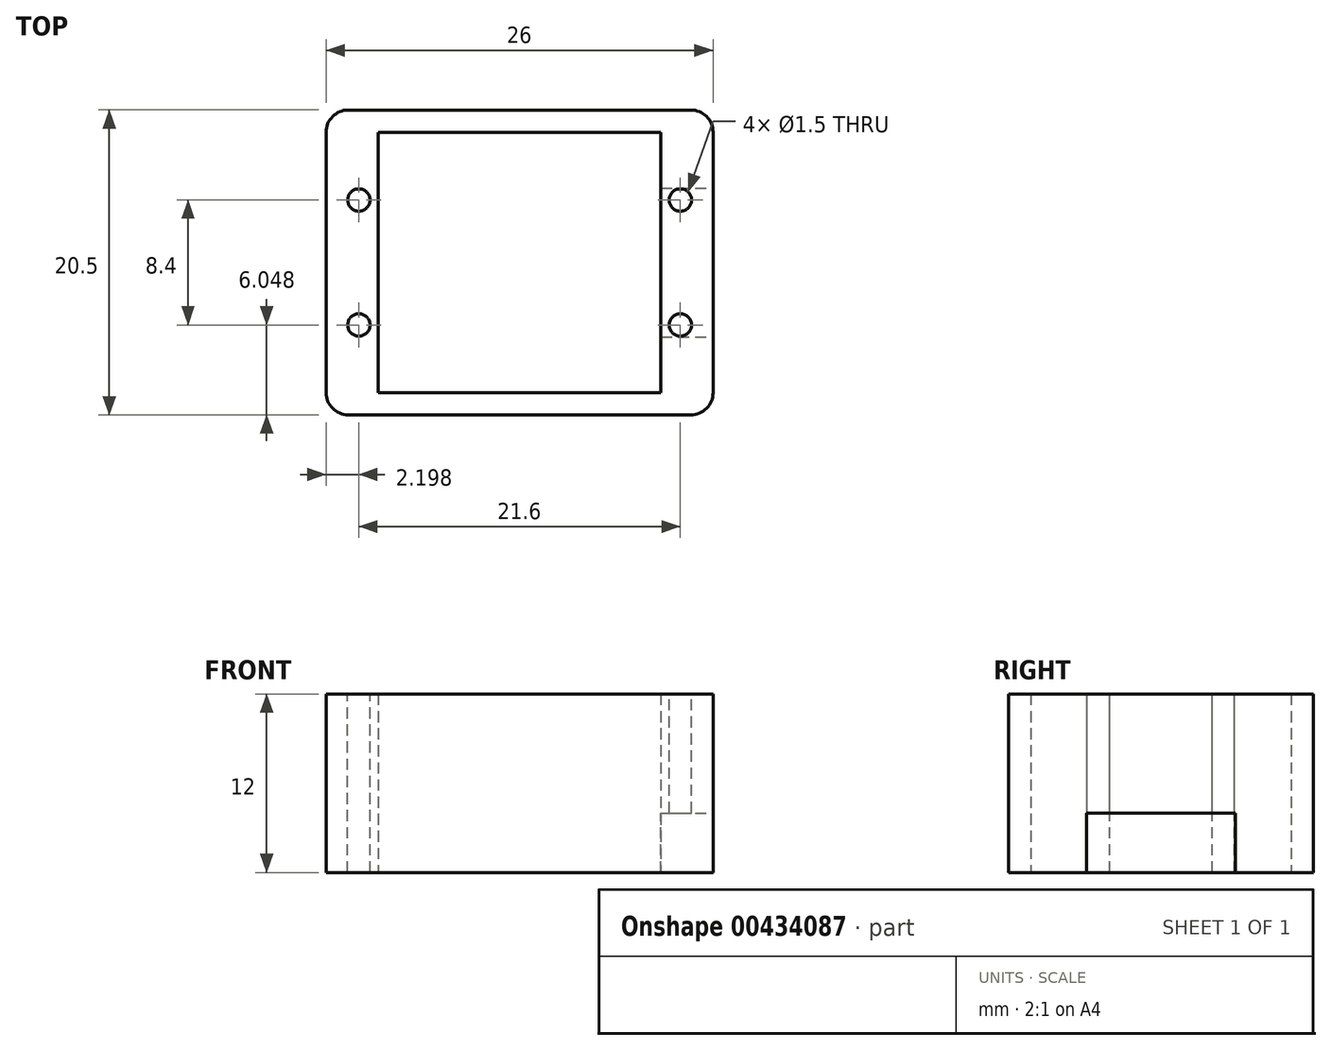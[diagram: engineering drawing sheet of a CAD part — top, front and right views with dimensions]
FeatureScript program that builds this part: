
annotation { "Feature Type Name" : "Feature", "Feature Type Description" : "" }
export const myFeature = defineFeature(function(context is Context, id is Id, definition is map)
    precondition{}
    {
        {
            var Q0;
            Q0=qCreatedBy(makeId("Top.planeOp"),FACE);
            var sketch = newSketch(context, id + "F0", { "sketchPlane" : qUnion([Q0])});
            skLineSegment(sketch, "E0.bottom", {"start": v(-15.26, 8.85) * mm, "end": v(10.74, 8.85) * mm});
            skLineSegment(sketch, "E0.top", {"start": v(-15.26, -11.65) * mm, "end": v(10.74, -11.65) * mm});
            skLineSegment(sketch, "E0.left", {"start": v(-15.26, 8.85) * mm, "end": v(-15.26, -11.65) * mm});
            skLineSegment(sketch, "E0.right", {"start": v(10.74, 8.85) * mm, "end": v(10.74, -11.65) * mm});
            skLineSegment(sketch, "E1.0", {"start": v(-11.76, 7.35) * mm, "end": v(5.74, 7.35) * mm});
            skLineSegment(sketch, "E2.0", {"start": v(-11.76, -10.15) * mm, "end": v(5.74, -10.15) * mm});
            skLineSegment(sketch, "E3.0", {"start": v(-11.76, 7.35) * mm, "end": v(-11.76, -10.15) * mm});
            skLineSegment(sketch, "E4.0", {"start": v(7.24, 7.35) * mm, "end": v(7.24, -10.15) * mm});
            skLineSegment(sketch, "E5.bottom", {"start": v(-11.76, 7.35) * mm, "end": v(7.24, 7.35) * mm});
            skLineSegment(sketch, "E5.top", {"start": v(-11.76, -10.15) * mm, "end": v(7.24, -10.15) * mm});
            skSolve(sketch);
        }
        {
            var Q0;
            Q0 = qSketchRegion(id + "F0", true);
            extrude(context, id + "F1", {"entities" : qUnion([Q0]), "depth" : 12 * mm, "offsetDistance" : 25 * mm});
        }
        {
            var Q0;
            Q0=makeQuery(id+"F1.opExtrude","SWEPT_FACE",FACE,{"disambiguationData":[OSD([sQuery(id+"F0.wireOp",EDGE,"E0.right")])]});
            var sketch = newSketch(context, id + "F2", { "sketchPlane" : qUnion([Q0])});
            skLineSegment(sketch, "E6", {"start": v(-1.4, 12) * mm, "end": v(-1.4, -4.28) * mm, "construction": true});
            skPoint(sketch, "E7.right.end.orphan", {"position": v(1.87, 4) * mm});
            skLineSegment(sketch, "E8.0", {"start": v(-6.4, 4) * mm, "end": v(-6.4, 0) * mm, "construction": true});
            skLineSegment(sketch, "E9.0", {"start": v(3.6, 4) * mm, "end": v(3.6, 0) * mm, "construction": true});
            skLineSegment(sketch, "E10.bottom", {"start": v(-6.4, 0) * mm, "end": v(3.6, 0) * mm});
            skLineSegment(sketch, "E10.top", {"start": v(-6.4, 4) * mm, "end": v(3.6, 4) * mm});
            skLineSegment(sketch, "E10.left", {"start": v(-6.4, 0) * mm, "end": v(-6.4, 4) * mm});
            skLineSegment(sketch, "E10.right", {"start": v(3.6, 0) * mm, "end": v(3.6, 4) * mm});
            skSolve(sketch);
        }
        {
            var Q0;
            Q0=makeQuery(id+"F1.opExtrude","SWEPT_EDGE",EDGE,{"disambiguationData":[OSD([sQuery(id+"F0.wireOp",EDGE,"E0.bottom"),sQuery(id+"F0.wireOp",EDGE,"E0.right")])]});
            var Q1;
            Q1=makeQuery(id+"F1.opExtrude","SWEPT_EDGE",EDGE,{"disambiguationData":[OSD([sQuery(id+"F0.wireOp",EDGE,"E0.top"),sQuery(id+"F0.wireOp",EDGE,"E0.right")])]});
            var Q2;
            Q2=makeQuery(id+"F1.opExtrude","SWEPT_EDGE",EDGE,{"disambiguationData":[OSD([sQuery(id+"F0.wireOp",EDGE,"E0.top"),sQuery(id+"F0.wireOp",EDGE,"E0.left")])]});
            var Q3;
            Q3=makeQuery(id+"F1.opExtrude","SWEPT_EDGE",EDGE,{"disambiguationData":[OSD([sQuery(id+"F0.wireOp",EDGE,"E0.bottom"),sQuery(id+"F0.wireOp",EDGE,"E0.left")])]});
            fillet(context, id + "F3", {"entities" : qUnion([Q0, Q1, Q2, Q3]), "radius" : 1.5 * mm, "tangentPropagation" : true, "allowEdgeOverflow" : false});
        }
        {
            var Q0;
            Q0=makeQuery(id+"F1.opExtrude","CAP_FACE",FACE,{"disambiguationData":[OSD([sQuery(id+"F0.wireOp",EDGE,"E0.bottom"),sQuery(id+"F0.wireOp",EDGE,"E0.top"),sQuery(id+"F0.wireOp",EDGE,"E0.left"),sQuery(id+"F0.wireOp",EDGE,"E0.right"),sQuery(id+"F0.wireOp",EDGE,"E5.bottom"),sQuery(id+"F0.wireOp",EDGE,"E5.top"),sQuery(id+"F0.wireOp",EDGE,"E3.0"),sQuery(id+"F0.wireOp",EDGE,"E4.0")])],"isStart":false});
            var sketch = newSketch(context, id + "F4", { "sketchPlane" : qUnion([Q0])});
            skLineSegment(sketch, "E11", {"start": v(-2.26, 7.35) * mm, "end": v(-2.26, -10.15) * mm, "construction": true});
            skLineSegment(sketch, "E12", {"start": v(-15.26, -1.4) * mm, "end": v(10.74, -1.4) * mm, "construction": true});
            skLineSegment(sketch, "E13.0", {"start": v(-15.26, -5.6) * mm, "end": v(10.74, -5.6) * mm, "construction": true});
            skLineSegment(sketch, "E14.0", {"start": v(-15.26, 2.8) * mm, "end": v(10.74, 2.8) * mm, "construction": true});
            skLineSegment(sketch, "E15.0", {"start": v(-13.06, 6.1) * mm, "end": v(-13.06, -8.9) * mm, "construction": true});
            skLineSegment(sketch, "E16.0", {"start": v(8.54, 6.1) * mm, "end": v(8.54, -8.9) * mm, "construction": true});
            skCircle(sketch, "E17", {"center": v(-13.06, 2.8) * mm, "radius": 0.75 * mm});
            skCircle(sketch, "E18", {"center": v(-13.06, -5.6) * mm, "radius": 0.75 * mm});
            skCircle(sketch, "E19", {"center": v(8.54, 2.8) * mm, "radius": 0.75 * mm});
            skCircle(sketch, "E20", {"center": v(8.54, -5.6) * mm, "radius": 0.75 * mm});
            skSolve(sketch);
        }
        {
            var Q0;
            Q0=sQuery(id+"F4.wireOp",VERTEX,"E17.center");
            var Q1;
            Q1=makeQuery(id+"F1.opExtrude","SWEPT_BODY",BODY,{"disambiguationData":[OSD([sQuery(id+"F0.wireOp",EDGE,"E0.bottom"),sQuery(id+"F0.wireOp",EDGE,"E0.top"),sQuery(id+"F0.wireOp",EDGE,"E0.left"),sQuery(id+"F0.wireOp",EDGE,"E0.right"),sQuery(id+"F0.wireOp",EDGE,"E5.bottom"),sQuery(id+"F0.wireOp",EDGE,"E5.top"),sQuery(id+"F0.wireOp",EDGE,"E3.0"),sQuery(id+"F0.wireOp",EDGE,"E4.0")])]});
            hole(context, id + "F5", {"style" : HoleStyle.SIMPLE, "endStyle" : HoleEndStyle.THROUGH, "holeDiameter" : 1.5 * mm, "isTappedThrough" : true, "tappedDepth" : 12 * mm, "tapClearance" : 3, "locations" : qUnion([Q0]), "scope" : qUnion([Q1])});
        }
        {
            var Q0;
            Q0=sQuery(id+"F4.wireOp",VERTEX,"E18.center");
            var Q1;
            Q1=makeQuery(id+"F1.opExtrude","SWEPT_BODY",BODY,{"disambiguationData":[OSD([sQuery(id+"F0.wireOp",EDGE,"E0.bottom"),sQuery(id+"F0.wireOp",EDGE,"E0.top"),sQuery(id+"F0.wireOp",EDGE,"E0.left"),sQuery(id+"F0.wireOp",EDGE,"E0.right"),sQuery(id+"F0.wireOp",EDGE,"E5.bottom"),sQuery(id+"F0.wireOp",EDGE,"E5.top"),sQuery(id+"F0.wireOp",EDGE,"E3.0"),sQuery(id+"F0.wireOp",EDGE,"E4.0")])]});
            hole(context, id + "F6", {"style" : HoleStyle.SIMPLE, "endStyle" : HoleEndStyle.THROUGH, "holeDiameter" : 1.5 * mm, "isTappedThrough" : true, "tappedDepth" : 12 * mm, "tapClearance" : 3, "locations" : qUnion([Q0]), "scope" : qUnion([Q1])});
        }
        {
            var Q0;
            Q0=sQuery(id+"F4.wireOp",VERTEX,"E20.center");
            var Q1;
            Q1=makeQuery(id+"F1.opExtrude","SWEPT_BODY",BODY,{"disambiguationData":[OSD([sQuery(id+"F0.wireOp",EDGE,"E0.bottom"),sQuery(id+"F0.wireOp",EDGE,"E0.top"),sQuery(id+"F0.wireOp",EDGE,"E0.left"),sQuery(id+"F0.wireOp",EDGE,"E0.right"),sQuery(id+"F0.wireOp",EDGE,"E5.bottom"),sQuery(id+"F0.wireOp",EDGE,"E5.top"),sQuery(id+"F0.wireOp",EDGE,"E3.0"),sQuery(id+"F0.wireOp",EDGE,"E4.0")])]});
            hole(context, id + "F7", {"style" : HoleStyle.SIMPLE, "endStyle" : HoleEndStyle.THROUGH, "holeDiameter" : 1.5 * mm, "isTappedThrough" : true, "tappedDepth" : 12 * mm, "tapClearance" : 3, "locations" : qUnion([Q0]), "scope" : qUnion([Q1])});
        }
        {
            var Q0;
            Q0=sQuery(id+"F4.wireOp",VERTEX,"E19.center");
            var Q1;
            Q1=makeQuery(id+"F1.opExtrude","SWEPT_BODY",BODY,{"disambiguationData":[OSD([sQuery(id+"F0.wireOp",EDGE,"E0.bottom"),sQuery(id+"F0.wireOp",EDGE,"E0.top"),sQuery(id+"F0.wireOp",EDGE,"E0.left"),sQuery(id+"F0.wireOp",EDGE,"E0.right"),sQuery(id+"F0.wireOp",EDGE,"E5.bottom"),sQuery(id+"F0.wireOp",EDGE,"E5.top"),sQuery(id+"F0.wireOp",EDGE,"E3.0"),sQuery(id+"F0.wireOp",EDGE,"E4.0")])]});
            hole(context, id + "F8", {"style" : HoleStyle.SIMPLE, "endStyle" : HoleEndStyle.THROUGH, "holeDiameter" : 1.5 * mm, "isTappedThrough" : true, "tappedDepth" : 12 * mm, "tapClearance" : 3, "locations" : qUnion([Q0]), "scope" : qUnion([Q1])});
        }
        {
            var Q0;
            Q0=makeQuery(id+"F2.imprint","IMPRINT",FACE,{"disambiguationData":[TD([[makeQuery(id+"F2.imprint","IMPRINT",EDGE,{"derivedFrom":sQuery(id+"F2.wireOp",EDGE,"E10.bottom")}),-1.0]])]});
            extrude(context, id + "F9", {"entities" : qUnion([Q0]), "operationType" : NewBodyOperationType.REMOVE, "oppositeDirection" : true, "depth" : 10 * mm, "offsetDistance" : 25 * mm});
        }
    });
